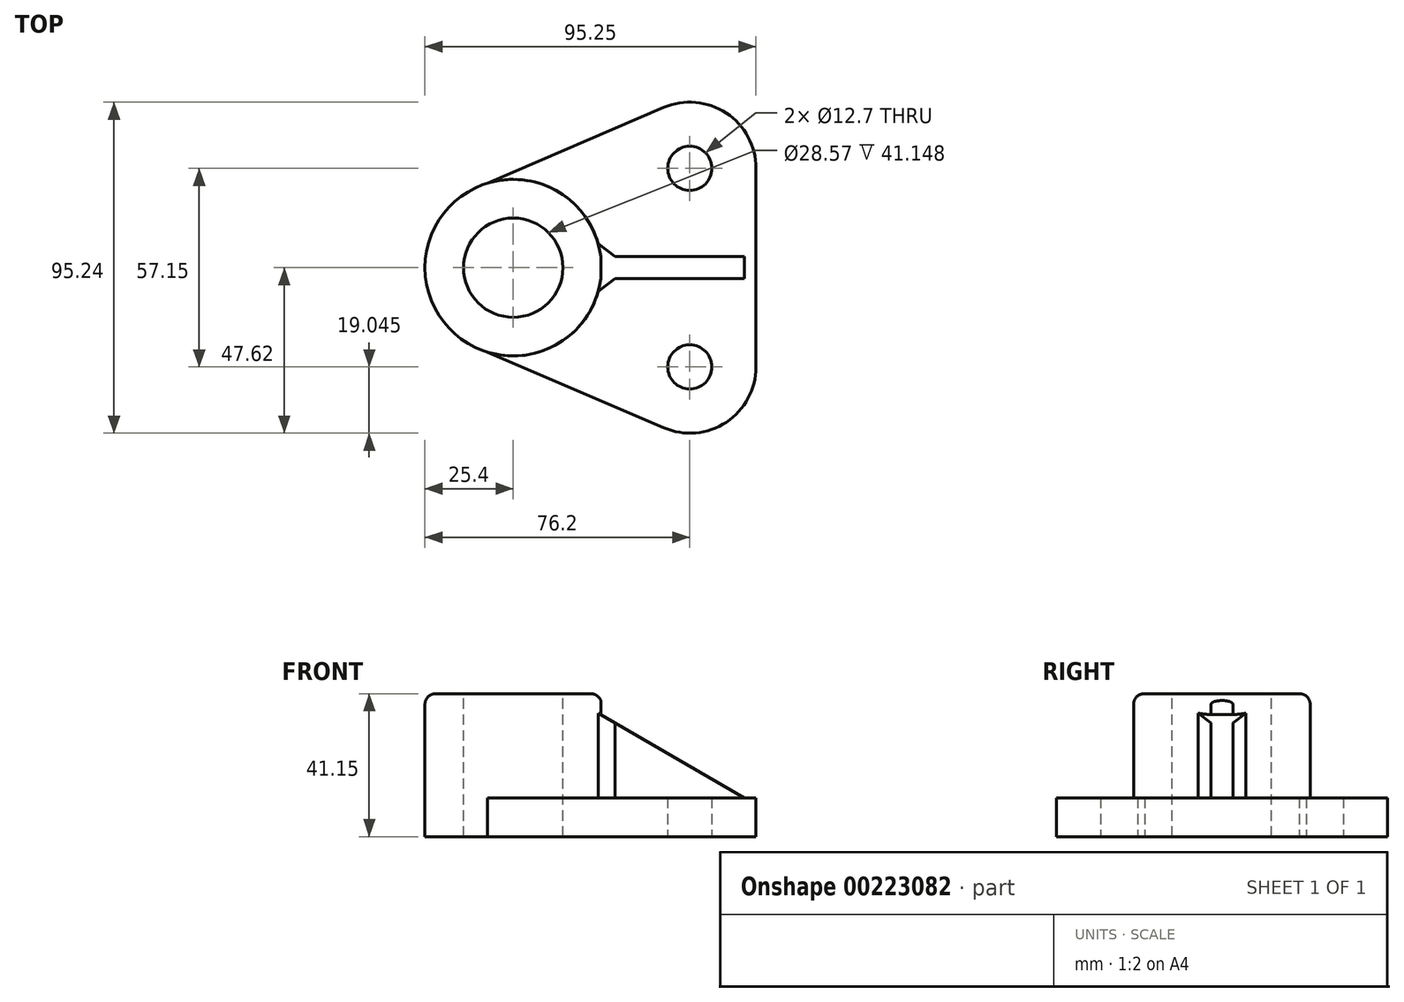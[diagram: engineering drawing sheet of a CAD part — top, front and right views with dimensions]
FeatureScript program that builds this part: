
annotation { "Feature Type Name" : "Feature", "Feature Type Description" : "" }
export const myFeature = defineFeature(function(context is Context, id is Id, definition is map)
    precondition{}
    {
        {
            var Q0;
            Q0=qCreatedBy(makeId("Top.planeOp"),FACE);
            var sketch = newSketch(context, id + "F0", { "sketchPlane" : qUnion([Q0])});
            skCircle(sketch, "E0", {"center": v(0, 0) * mm, "radius": 25.4 * mm});
            skLineSegment(sketch, "E1", {"start": v(0, 0) * mm, "end": v(50.8, 0) * mm, "construction": true});
            skLineSegment(sketch, "E2", {"start": v(50.8, 0) * mm, "end": v(50.8, 28.58) * mm, "construction": true});
            skCircle(sketch, "E3", {"center": v(50.8, 28.58) * mm, "radius": 6.35 * mm});
            skArc(sketch, "E4", {"start": v(69.85, 28.58) * mm, "mid": v(61.28, 44.48) * mm, "end": v(43.28, 46.08) * mm});
            skLineSegment(sketch, "E5", {"start": v(-7.4, 24.3) * mm, "end": v(43.28, 46.08) * mm});
            skLineSegment(sketch, "E6", {"start": v(69.85, 28.58) * mm, "end": v(69.85, -30.95) * mm});
            skCircle(sketch, "E7.MirrorC", {"center": v(50.8, -28.58) * mm, "radius": 6.35 * mm});
            skArc(sketch, "E8.MirrorC", {"start": v(69.85, -28.58) * mm, "mid": v(61.28, -44.48) * mm, "end": v(43.28, -46.08) * mm});
            skLineSegment(sketch, "E9.MirrorCS", {"start": v(-7.4, -24.3) * mm, "end": v(43.28, -46.08) * mm});
            skSolve(sketch);
        }
        {
            var Q0;
            Q0 = qSketchRegion(id + "F0", true);
            extrude(context, id + "F1", {"entities" : qUnion([Q0]), "depth" : 11.18 * mm});
        }
        {
            var Q0;
            Q0=makeQuery(id+"F1.opExtrude","CAP_FACE",FACE,{"disambiguationData":[OSD([sQuery(id+"F0.wireOp",EDGE,"E0"),sQuery(id+"F0.wireOp",EDGE,"E3"),sQuery(id+"F0.wireOp",EDGE,"E4"),sQuery(id+"F0.wireOp",EDGE,"E5"),sQuery(id+"F0.wireOp",EDGE,"E6"),sQuery(id+"F0.wireOp",EDGE,"E7.MirrorC"),sQuery(id+"F0.wireOp",EDGE,"E8.MirrorC"),sQuery(id+"F0.wireOp",EDGE,"E9.MirrorCS")])],"isStart":false});
            var sketch = newSketch(context, id + "F2", { "sketchPlane" : qUnion([Q0])});
            skArc(sketch, "E10", {"start": v(25.2, 3.18) * mm, "mid": v(-25.4, 0) * mm, "end": v(25.2, -3.18) * mm});
            skLineSegment(sketch, "E11", {"start": v(69.85, 0) * mm, "end": v(66.55, 0) * mm});
            skPoint(sketch, "E11.endSnap0", {"position": v(69.85, 0) * mm});
            skLineSegment(sketch, "E12", {"start": v(66.55, 0) * mm, "end": v(66.55, 3.18) * mm});
            skLineSegment(sketch, "E13.bottom", {"start": v(25.4, -3.18) * mm, "end": v(66.55, -3.18) * mm});
            skLineSegment(sketch, "E13.top", {"start": v(25.4, 3.18) * mm, "end": v(66.55, 3.18) * mm});
            skLineSegment(sketch, "E13.right", {"start": v(66.55, -3.18) * mm, "end": v(66.55, 3.18) * mm});
            skLineSegment(sketch, "E14", {"start": v(25.4, 3.18) * mm, "end": v(25.2, 3.18) * mm});
            skLineSegment(sketch, "E15", {"start": v(25.4, -3.18) * mm, "end": v(25.2, -3.18) * mm});
            skPoint(sketch, "E16.start.orphan", {"position": v(25.4, 0) * mm});
            skPoint(sketch, "E17.orphan", {"position": v(16.6, -3.18) * mm});
            skPoint(sketch, "E18.orphan", {"position": v(16.6, 3.18) * mm});
            skSolve(sketch);
        }
        {
            var Q0;
            Q0 = qSketchRegion(id + "F2", true);
            extrude(context, id + "F3", {"entities" : qUnion([Q0]), "operationType" : NewBodyOperationType.ADD, "depth" : 29.97 * mm});
        }
        {
            var Q0;
            Q0=makeQuery(id+"F3.opExtrude","SWEPT_FACE",FACE,{"disambiguationData":[OSD([sQuery(id+"F2.wireOp",EDGE,"E13.bottom"),sQuery(id+"F2.wireOp",EDGE,"E15")])]});
            var sketch = newSketch(context, id + "F4", { "sketchPlane" : qUnion([Q0])});
            skLineSegment(sketch, "E19", {"start": v(25.2, 11.18) * mm, "end": v(66.55, 11.18) * mm});
            skLineSegment(sketch, "E20", {"start": v(66.55, 11.18) * mm, "end": v(66.55, 41.15) * mm});
            skLineSegment(sketch, "E21", {"start": v(66.55, 11.18) * mm, "end": v(25.2, 35.1) * mm});
            skLineSegment(sketch, "E22", {"start": v(25.2, 35.1) * mm, "end": v(25.2, 41.15) * mm});
            skLineSegment(sketch, "E23", {"start": v(25.2, 41.15) * mm, "end": v(66.55, 41.15) * mm});
            skLineSegment(sketch, "E24", {"start": v(66.55, 41.15) * mm, "end": v(66.55, 11.18) * mm});
            skSolve(sketch);
        }
        {
            var Q0;
            Q0 = qSketchRegion(id + "F4", true);
            extrude(context, id + "F5", {"entities" : qUnion([Q0]), "operationType" : NewBodyOperationType.REMOVE, "oppositeDirection" : true, "depth" : 25.4 * mm});
        }
        {
            var Q0;
            Q0=makeQuery(id+"F3.opExtrude","CAP_FACE",FACE,{"disambiguationData":[OSD([sQuery(id+"F2.wireOp",EDGE,"E10"),sQuery(id+"F2.wireOp",EDGE,"E13.bottom"),sQuery(id+"F2.wireOp",EDGE,"E13.top"),sQuery(id+"F2.wireOp",EDGE,"E13.right"),sQuery(id+"F2.wireOp",EDGE,"E14"),sQuery(id+"F2.wireOp",EDGE,"E15")])],"isStart":false});
            var sketch = newSketch(context, id + "F6", { "sketchPlane" : qUnion([Q0])});
            skCircle(sketch, "E25", {"center": v(0, 0) * mm, "radius": 14.29 * mm});
            skSolve(sketch);
        }
        {
            var Q0;
            Q0 = qSketchRegion(id + "F6", true);
            extrude(context, id + "F7", {"entities" : qUnion([Q0]), "operationType" : NewBodyOperationType.REMOVE, "oppositeDirection" : true, "depth" : 100.33 * mm});
        }
        {
            var Q0;
            Q0=makeQuery(id+"F3.opExtrude","CAP_EDGE",EDGE,{"disambiguationData":[OSD([sQuery(id+"F2.wireOp",EDGE,"E10")])],"isStart":false});
            fillet(context, id + "F8", {"entities" : qUnion([Q0]), "radius" : 3.05 * mm, "tangentPropagation" : true, "allowEdgeOverflow" : false});
        }
        {
            var Q0;
            Q0=makeQuery(id+"F3.opExtrude","CAP_EDGE",EDGE,{"disambiguationData":[OSD([sQuery(id+"F2.wireOp",EDGE,"E13.bottom"),sQuery(id+"F2.wireOp",EDGE,"E15")])],"isStart":true});
            var Q1;
            {var subQ0=sQuery(id+"F0.wireOp",EDGE,"E9.MirrorCS");var subQ2=sQuery(id+"F2.wireOp",EDGE,"E10");Q1=makeQuery(id+"F3.boolean.opBoolean","SPLIT",EDGE,{"disambiguationData":[TD([makeQuery(id+"F1.opExtrude","SWEPT_FACE",FACE,{"disambiguationData":[OSD([subQ0])]})])],"derivedFrom":makeQuery(id+"F3.opExtrude","CAP_EDGE",EDGE,{"disambiguationData":[OSD([subQ2])],"isStart":true})});}
            var Q2;
            Q2=makeQuery(id+"F5.boolean.opBoolean","SPLIT",EDGE,{"derivedFrom":makeQuery(id+"F3.opExtrude","SWEPT_EDGE",EDGE,{"disambiguationData":[OSD([sQuery(id+"F2.wireOp",EDGE,"E10"),sQuery(id+"F2.wireOp",EDGE,"E15")])]})});
            var Q3;
            {var subQ0=sQuery(id+"F0.wireOp",EDGE,"E5");var subQ1=sQuery(id+"F2.wireOp",EDGE,"E10");Q3=makeQuery(id+"F3.boolean.opBoolean","SPLIT",EDGE,{"disambiguationData":[TD([makeQuery(id+"F1.opExtrude","SWEPT_FACE",FACE,{"disambiguationData":[OSD([subQ0])]})])],"derivedFrom":makeQuery(id+"F3.opExtrude","CAP_EDGE",EDGE,{"disambiguationData":[OSD([subQ1])],"isStart":true})});}
            var Q4;
            Q4=makeQuery(id+"F3.opExtrude","CAP_EDGE",EDGE,{"disambiguationData":[OSD([sQuery(id+"F2.wireOp",EDGE,"E13.top"),sQuery(id+"F2.wireOp",EDGE,"E14")])],"isStart":true});
            var Q5;
            {var subQ0=sQuery(id+"F2.wireOp",EDGE,"E14");var subQ1=sQuery(id+"F0.wireOp",EDGE,"E0");var subQ2=sQuery(id+"F2.wireOp",EDGE,"E10");Q5=makeQuery(id+"F5.boolean.opBoolean","SPLIT",EDGE,{"disambiguationData":[TD([makeQuery(id+"F1.opExtrude","CAP_FACE",FACE,{"disambiguationData":[OSD([subQ1,sQuery(id+"F0.wireOp",EDGE,"E3"),sQuery(id+"F0.wireOp",EDGE,"E4"),sQuery(id+"F0.wireOp",EDGE,"E5"),sQuery(id+"F0.wireOp",EDGE,"E6"),sQuery(id+"F0.wireOp",EDGE,"E7.MirrorC"),sQuery(id+"F0.wireOp",EDGE,"E8.MirrorC"),sQuery(id+"F0.wireOp",EDGE,"E9.MirrorCS")])],"isStart":false})])],"derivedFrom":makeQuery(id+"F3.opExtrude","SWEPT_EDGE",EDGE,{"disambiguationData":[OSD([subQ2,subQ0])]})});}
            chamfer(context, id + "F9", {"entities" : qUnion([Q0, Q1, Q2, Q3, Q4, Q5]), "width" : 5.08 * mm, "tangentPropagation" : true});
        }
    });
